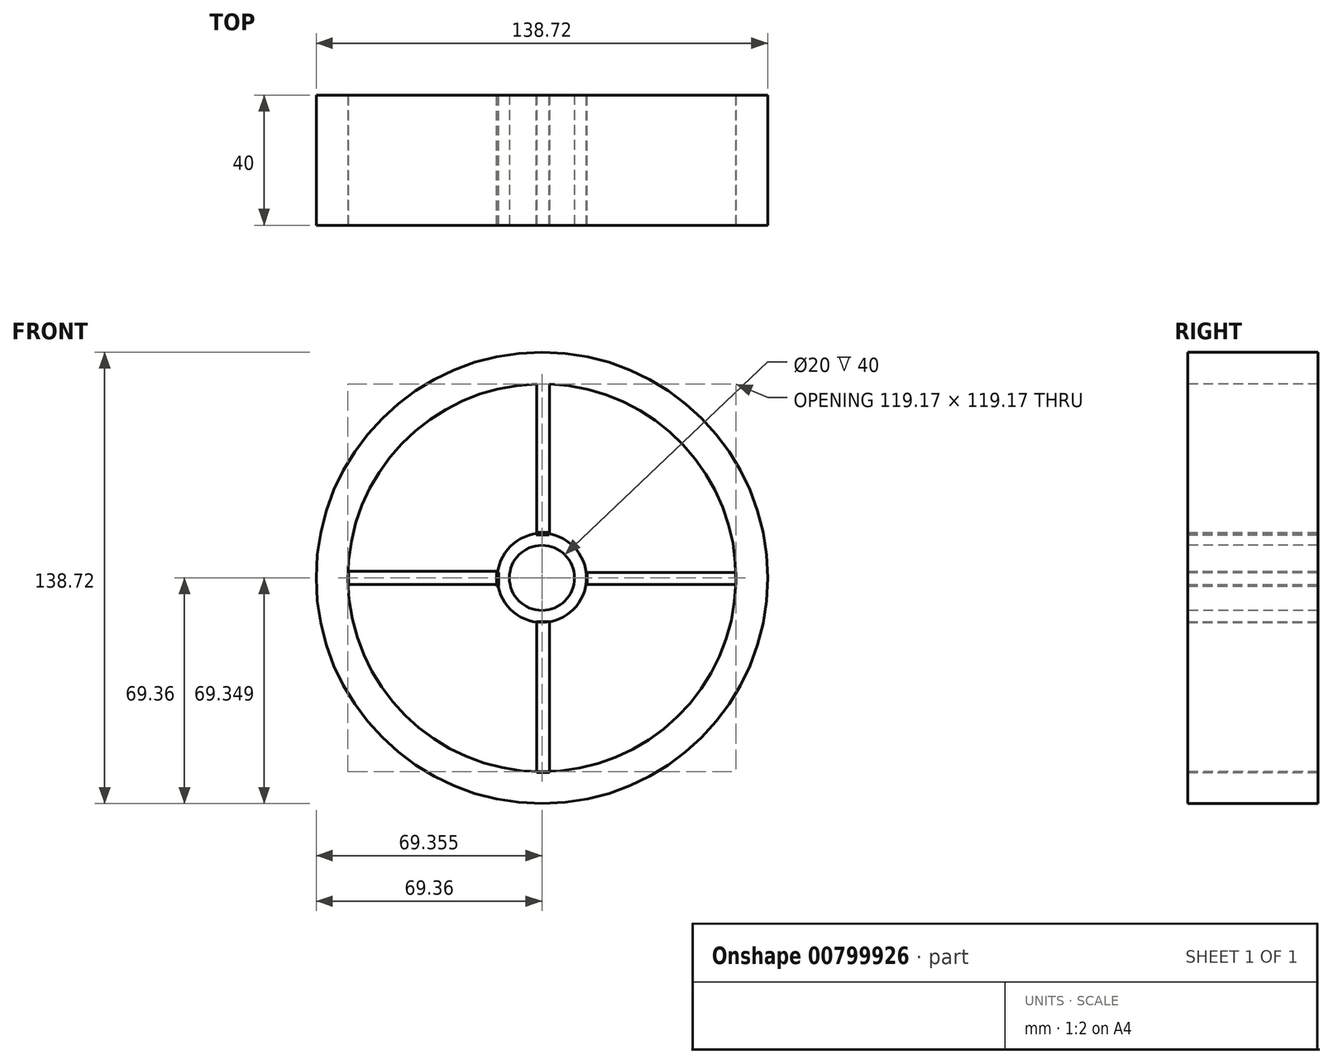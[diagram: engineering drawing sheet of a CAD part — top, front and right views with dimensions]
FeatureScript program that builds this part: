
annotation { "Feature Type Name" : "Feature", "Feature Type Description" : "" }
export const myFeature = defineFeature(function(context is Context, id is Id, definition is map)
    precondition{}
    {
        {
            var Q0;
            Q0=qCreatedBy(makeId("Front.planeOp"),FACE);
            var sketch = newSketch(context, id + "F0", { "sketchPlane" : qUnion([Q0])});
            skCircle(sketch, "E0", {"center": v(0, 0) * mm, "radius": 69.36 * mm});
            skSolve(sketch);
        }
        {
            var Q0;
            Q0=qCreatedBy(makeId("Front.planeOp"),FACE);
            var sketch = newSketch(context, id + "F1", { "sketchPlane" : qUnion([Q0])});
            skCircle(sketch, "E1", {"center": v(0, 0) * mm, "radius": 13.7 * mm});
            skSolve(sketch);
        }
        {
            var Q0;
            Q0=makeQuery(id+"F0.imprint","IMPRINT",FACE,{"disambiguationData":[TD([[makeQuery(id+"F0.imprint","IMPRINT",EDGE,{"derivedFrom":sQuery(id+"F0.wireOp",EDGE,"E0")}),1.0]])]});
            extrude(context, id + "F2", {"entities" : qUnion([Q0]), "depth" : 40 * mm, "offsetDistance" : 25.4 * mm});
        }
        {
            var Q0;
            Q0=makeQuery(id+"F2.opExtrude","CAP_FACE",FACE,{"disambiguationData":[OSD([sQuery(id+"F0.wireOp",EDGE,"E0")])],"isStart":false});
            var sketch = newSketch(context, id + "F3", { "sketchPlane" : qUnion([Q0])});
            skCircle(sketch, "E2", {"center": v(0, 0) * mm, "radius": 59.6 * mm});
            skSolve(sketch);
        }
        {
            var Q0;
            Q0=makeQuery(id+"F3.imprint","IMPRINT",FACE,{"disambiguationData":[TD([[makeQuery(id+"F3.imprint","IMPRINT",EDGE,{"derivedFrom":sQuery(id+"F3.wireOp",EDGE,"E2")}),1.0]])]});
            extrude(context, id + "F4", {"entities" : qUnion([Q0]), "operationType" : NewBodyOperationType.REMOVE, "oppositeDirection" : true, "depth" : 40 * mm, "offsetDistance" : 25.4 * mm});
        }
        {
            var Q0;
            Q0=makeQuery(id+"F1.imprint","IMPRINT",FACE,{"disambiguationData":[TD([[makeQuery(id+"F1.imprint","IMPRINT",EDGE,{"derivedFrom":sQuery(id+"F1.wireOp",EDGE,"E1")}),1.0]])]});
            extrude(context, id + "F5", {"entities" : qUnion([Q0]), "depth" : 40 * mm, "offsetDistance" : 25.4 * mm});
        }
        {
            var Q0;
            Q0=qCreatedBy(makeId("Front.planeOp"),FACE);
            var sketch = newSketch(context, id + "F6", { "sketchPlane" : qUnion([Q0])});
            skLineSegment(sketch, "E3.bottom", {"start": v(-1.68, 13.9) * mm, "end": v(2.27, 13.9) * mm});
            skLineSegment(sketch, "E3.top", {"start": v(-1.68, 59.81) * mm, "end": v(2.27, 59.81) * mm});
            skLineSegment(sketch, "E3.left", {"start": v(-1.68, 13.9) * mm, "end": v(-1.68, 59.81) * mm});
            skLineSegment(sketch, "E3.right", {"start": v(2.27, 13.9) * mm, "end": v(2.27, 59.81) * mm});
            skFitSpline(sketch, "E4", {"points": [v(-1.68, 13.9) * mm, v(-19.41, 56.07) * mm, v(-35.57, 47.99) * mm, v(-35.77, 48.18) * mm, v(-35.37, 48.18) * mm], "startDerivative": vector(-21.19, 113.53) * mm, "endDerivative": vector(10.26, -2.03) * mm});
            skFitSpline(sketch, "E5", {"points": [v(2.27, 13.9) * mm, v(20.6, 56.07) * mm, v(41.48, 43.06) * mm, v(42.07, 43.06) * mm], "startDerivative": vector(21.9, 117.47) * mm, "endDerivative": vector(6.14, 4.15) * mm});
            skSolve(sketch);
        }
        {
            var Q0;
            Q0 = qSketchRegion(id + "F6", true);
            extrude(context, id + "F7", {"entities" : qUnion([Q0]), "operationType" : NewBodyOperationType.ADD, "depth" : 40 * mm, "offsetDistance" : 25.4 * mm});
        }
        {
            var Q0;
            Q0=qCreatedBy(makeId("Front.planeOp"),FACE);
            var sketch = newSketch(context, id + "F8", { "sketchPlane" : qUnion([Q0])});
            skLineSegment(sketch, "E6.bottom", {"start": v(-1.68, -13.5) * mm, "end": v(2.27, -13.5) * mm});
            skLineSegment(sketch, "E6.top", {"start": v(-1.68, -59.81) * mm, "end": v(2.27, -59.81) * mm});
            skLineSegment(sketch, "E6.left", {"start": v(-1.68, -13.5) * mm, "end": v(-1.68, -59.81) * mm});
            skLineSegment(sketch, "E6.right", {"start": v(2.27, -13.5) * mm, "end": v(2.27, -59.81) * mm});
            skLineSegment(sketch, "E7.bottom", {"start": v(-13.9, 2.07) * mm, "end": v(-59.42, 2.07) * mm});
            skLineSegment(sketch, "E7.top", {"start": v(-13.9, -2.07) * mm, "end": v(-59.42, -2.07) * mm});
            skLineSegment(sketch, "E7.left", {"start": v(-13.9, 2.07) * mm, "end": v(-13.9, -2.07) * mm});
            skLineSegment(sketch, "E7.right", {"start": v(-59.42, 2.07) * mm, "end": v(-59.42, -2.07) * mm});
            skLineSegment(sketch, "E8.bottom", {"start": v(13.9, 1.68) * mm, "end": v(59.61, 1.68) * mm});
            skLineSegment(sketch, "E8.top", {"start": v(13.9, -2.07) * mm, "end": v(59.61, -2.07) * mm});
            skLineSegment(sketch, "E8.left", {"start": v(13.9, 1.68) * mm, "end": v(13.9, -2.07) * mm});
            skLineSegment(sketch, "E8.right", {"start": v(59.61, 1.68) * mm, "end": v(59.61, -2.07) * mm});
            skSolve(sketch);
        }
        {
            var Q0;
            Q0=makeQuery(id+"F8.imprint","IMPRINT",FACE,{"disambiguationData":[TD([[makeQuery(id+"F8.imprint","IMPRINT",EDGE,{"derivedFrom":sQuery(id+"F8.wireOp",EDGE,"E7.bottom")}),1.0]])]});
            var Q1;
            Q1=makeQuery(id+"F8.imprint","IMPRINT",FACE,{"disambiguationData":[TD([[makeQuery(id+"F8.imprint","IMPRINT",EDGE,{"derivedFrom":sQuery(id+"F8.wireOp",EDGE,"E8.bottom")}),-1.0]])]});
            var Q2;
            Q2=makeQuery(id+"F8.imprint","IMPRINT",FACE,{"disambiguationData":[TD([[makeQuery(id+"F8.imprint","IMPRINT",EDGE,{"derivedFrom":sQuery(id+"F8.wireOp",EDGE,"E6.bottom")}),-1.0]])]});
            extrude(context, id + "F9", {"entities" : qUnion([Q0, Q1, Q2]), "depth" : 40 * mm, "offsetDistance" : 25.4 * mm});
        }
        {
            var Q0;
            Q0=makeQuery(id+"F5.opExtrude","CAP_FACE",FACE,{"disambiguationData":[OSD([sQuery(id+"F1.wireOp",EDGE,"E1")])],"isStart":false});
            var sketch = newSketch(context, id + "F10", { "sketchPlane" : qUnion([Q0])});
            skCircle(sketch, "E9", {"center": v(0, 0) * mm, "radius": 9.94 * mm});
            skSolve(sketch);
        }
        {
            var Q0;
            Q0=sQuery(id+"F10.wireOp",VERTEX,"E9.center");
            var Q1;
            Q1=makeQuery(id+"F5.opExtrude","SWEPT_BODY",BODY,{"disambiguationData":[OSD([sQuery(id+"F1.wireOp",EDGE,"E1")])]});
            hole(context, id + "F11", {"style" : HoleStyle.SIMPLE, "endStyle" : HoleEndStyle.THROUGH, "holeDiameter" : 20 * mm, "majorDiameter" : 6.35 * mm, "isTappedThrough" : true, "tappedDepth" : 12.7 * mm, "tapClearance" : 3, "locations" : qUnion([Q0]), "scope" : qUnion([Q1])});
        }
        {
            var Q0;
            Q0=qCreatedBy(makeId("Front.planeOp"),FACE);
            var sketch = newSketch(context, id + "F12", { "sketchPlane" : qUnion([Q0])});
            skLineSegment(sketch, "E10.bottom", {"start": v(13.9, 1.68) * mm, "end": v(13.58, 1.68) * mm});
            skLineSegment(sketch, "E10.top", {"start": v(13.9, -2.06) * mm, "end": v(13.58, -2.06) * mm});
            skLineSegment(sketch, "E10.left", {"start": v(13.9, 1.68) * mm, "end": v(13.9, -2.06) * mm});
            skLineSegment(sketch, "E10.right", {"start": v(13.58, 1.68) * mm, "end": v(13.58, -2.06) * mm});
            skLineSegment(sketch, "E11.bottom", {"start": v(2.25, 13.96) * mm, "end": v(-1.69, 13.96) * mm});
            skLineSegment(sketch, "E11.top", {"start": v(2.25, 13.22) * mm, "end": v(-1.69, 13.22) * mm});
            skLineSegment(sketch, "E11.left", {"start": v(2.25, 13.96) * mm, "end": v(2.25, 13.22) * mm});
            skLineSegment(sketch, "E11.right", {"start": v(-1.69, 13.96) * mm, "end": v(-1.69, 13.22) * mm});
            skLineSegment(sketch, "E12.bottom", {"start": v(-13.88, 1.6) * mm, "end": v(-13.36, 1.6) * mm});
            skLineSegment(sketch, "E12.top", {"start": v(-13.88, -2.54) * mm, "end": v(-13.36, -2.54) * mm});
            skLineSegment(sketch, "E12.left", {"start": v(-13.88, 1.6) * mm, "end": v(-13.88, -2.54) * mm});
            skLineSegment(sketch, "E12.right", {"start": v(-13.36, 1.6) * mm, "end": v(-13.36, -2.54) * mm});
            skSolve(sketch);
        }
        {
            var Q0;
            Q0 = qSketchRegion(id + "F12", true);
            extrude(context, id + "F13", {"entities" : qUnion([Q0]), "depth" : 40 * mm, "offsetDistance" : 25.4 * mm});
        }
    });
